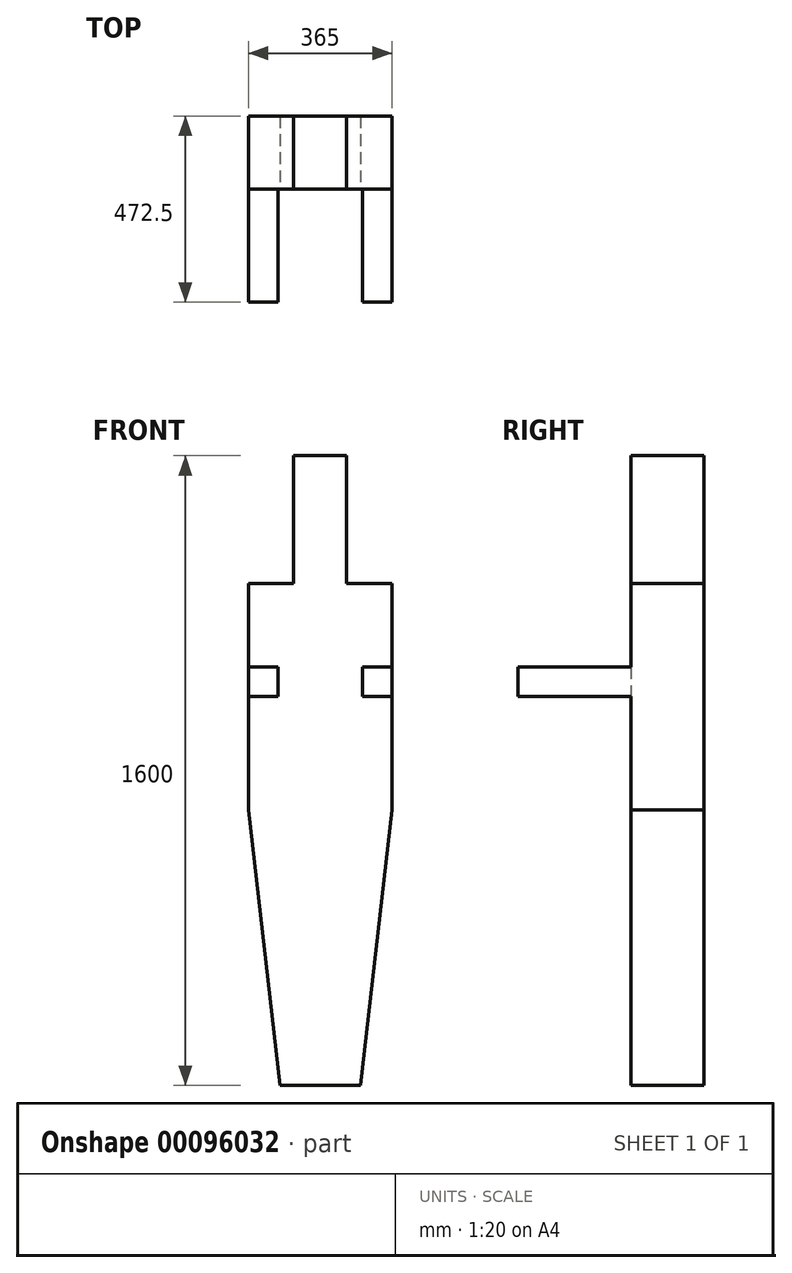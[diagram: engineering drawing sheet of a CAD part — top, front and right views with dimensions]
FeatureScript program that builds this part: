
annotation { "Feature Type Name" : "Feature", "Feature Type Description" : "" }
export const myFeature = defineFeature(function(context is Context, id is Id, definition is map)
    precondition{}
    {
        {
            var Q0;
            Q0=qCreatedBy(makeId("Top.planeOp"),FACE);
            var sketch = newSketch(context, id + "F0", { "sketchPlane" : qUnion([Q0])});
            skLineSegment(sketch, "E0.bottom", {"start": v(182.5, -92.5) * mm, "end": v(-182.5, -92.5) * mm});
            skLineSegment(sketch, "E0.top", {"start": v(182.5, 92.5) * mm, "end": v(-182.5, 92.5) * mm});
            skLineSegment(sketch, "E0.left", {"start": v(182.5, -92.5) * mm, "end": v(182.5, 92.5) * mm});
            skLineSegment(sketch, "E0.right", {"start": v(-182.5, -92.5) * mm, "end": v(-182.5, 92.5) * mm});
            skPoint(sketch, "E0.middle", {"position": v(0, 0) * mm});
            skSolve(sketch);
        }
        {
            var Q0;
            Q0 = qSketchRegion(id + "F0", true);
            extrude(context, id + "F1", {"entities" : qUnion([Q0]), "depth" : 1600 * mm});
        }
        {
            var Q0;
            Q0=qCreatedBy(makeId("Front.planeOp"),FACE);
            var sketch = newSketch(context, id + "F2", { "sketchPlane" : qUnion([Q0])});
            skLineSegment(sketch, "E1.bottom", {"start": v(-107.5, 987.5) * mm, "end": v(-182.5, 987.5) * mm});
            skLineSegment(sketch, "E1.top", {"start": v(-107.5, 1062.5) * mm, "end": v(-182.5, 1062.5) * mm});
            skLineSegment(sketch, "E1.left", {"start": v(-107.5, 987.5) * mm, "end": v(-107.5, 1062.5) * mm});
            skLineSegment(sketch, "E1.right", {"start": v(-182.5, 987.5) * mm, "end": v(-182.5, 1062.5) * mm});
            skPoint(sketch, "E1.middle", {"position": v(-145, 1025) * mm});
            skLineSegment(sketch, "E2.MirrorCS", {"start": v(107.5, 987.5) * mm, "end": v(107.5, 1062.5) * mm});
            skLineSegment(sketch, "E3.MirrorCS", {"start": v(107.5, 1062.5) * mm, "end": v(182.5, 1062.5) * mm});
            skLineSegment(sketch, "E4.MirrorCS", {"start": v(182.5, 987.5) * mm, "end": v(182.5, 1062.5) * mm});
            skLineSegment(sketch, "E5.MirrorCS", {"start": v(107.5, 987.5) * mm, "end": v(182.5, 987.5) * mm});
            skSolve(sketch);
        }
        {
            var Q0;
            Q0 = qSketchRegion(id + "F2", true);
            extrude(context, id + "F3", {"entities" : qUnion([Q0]), "operationType" : NewBodyOperationType.ADD, "depth" : (220 + 160) * mm});
        }
        {
            var Q0;
            Q0=makeQuery(id+"F1.opExtrude","CAP_FACE",FACE,{"disambiguationData":[OSD([sQuery(id+"F0.wireOp",EDGE,"E0.bottom"),sQuery(id+"F0.wireOp",EDGE,"E0.top"),sQuery(id+"F0.wireOp",EDGE,"E0.left"),sQuery(id+"F0.wireOp",EDGE,"E0.right")])],"isStart":false});
            var sketch = newSketch(context, id + "F4", { "sketchPlane" : qUnion([Q0])});
            skPoint(sketch, "E6.middle", {"position": v(0, 0) * mm});
            skLineSegment(sketch, "E7.bottom", {"start": v(-182.5, 92.5) * mm, "end": v(-67.5, 92.5) * mm});
            skLineSegment(sketch, "E7.top", {"start": v(-182.5, -92.5) * mm, "end": v(-67.5, -92.5) * mm});
            skLineSegment(sketch, "E7.left", {"start": v(-182.5, 92.5) * mm, "end": v(-182.5, -92.5) * mm});
            skLineSegment(sketch, "E7.right", {"start": v(-67.5, 92.5) * mm, "end": v(-67.5, -92.5) * mm});
            skLineSegment(sketch, "E8.bottom", {"start": v(182.5, 92.5) * mm, "end": v(67.5, 92.5) * mm});
            skLineSegment(sketch, "E8.top", {"start": v(182.5, -92.5) * mm, "end": v(67.5, -92.5) * mm});
            skLineSegment(sketch, "E8.left", {"start": v(182.5, 92.5) * mm, "end": v(182.5, -92.5) * mm});
            skLineSegment(sketch, "E8.right", {"start": v(67.5, 92.5) * mm, "end": v(67.5, -92.5) * mm});
            skSolve(sketch);
        }
        {
            var Q0;
            Q0 = qSketchRegion(id + "F4", true);
            extrude(context, id + "F5", {"entities" : qUnion([Q0]), "operationType" : NewBodyOperationType.REMOVE, "oppositeDirection" : true, "depth" : 325 * mm});
        }
        {
            var Q0;
            Q0=makeQuery(id+"F1.opExtrude","SWEPT_FACE",FACE,{"disambiguationData":[OSD([sQuery(id+"F0.wireOp",EDGE,"E0.bottom")])]});
            var sketch = newSketch(context, id + "F6", { "sketchPlane" : qUnion([Q0])});
            skLineSegment(sketch, "E9", {"start": v(-182.5, 700) * mm, "end": v(-102.5, 0) * mm});
            skLineSegment(sketch, "E10", {"start": v(-102.5, 0) * mm, "end": v(-182.5, 0) * mm});
            skLineSegment(sketch, "E11", {"start": v(-182.5, 0) * mm, "end": v(-182.5, 700) * mm});
            skLineSegment(sketch, "E12.MirrorCS", {"start": v(182.5, 700) * mm, "end": v(102.5, 0) * mm});
            skLineSegment(sketch, "E13.MirrorCS", {"start": v(102.5, 0) * mm, "end": v(182.5, 0) * mm});
            skLineSegment(sketch, "E14.MirrorCS", {"start": v(182.5, 0) * mm, "end": v(182.5, 700) * mm});
            skSolve(sketch);
        }
        {
            var Q0;
            Q0 = qSketchRegion(id + "F6", true);
            extrude(context, id + "F7", {"entities" : qUnion([Q0]), "operationType" : NewBodyOperationType.REMOVE, "endBound" : BoundingType.THROUGH_ALL, "oppositeDirection" : true, "depth" : 25 * mm});
        }
    });
